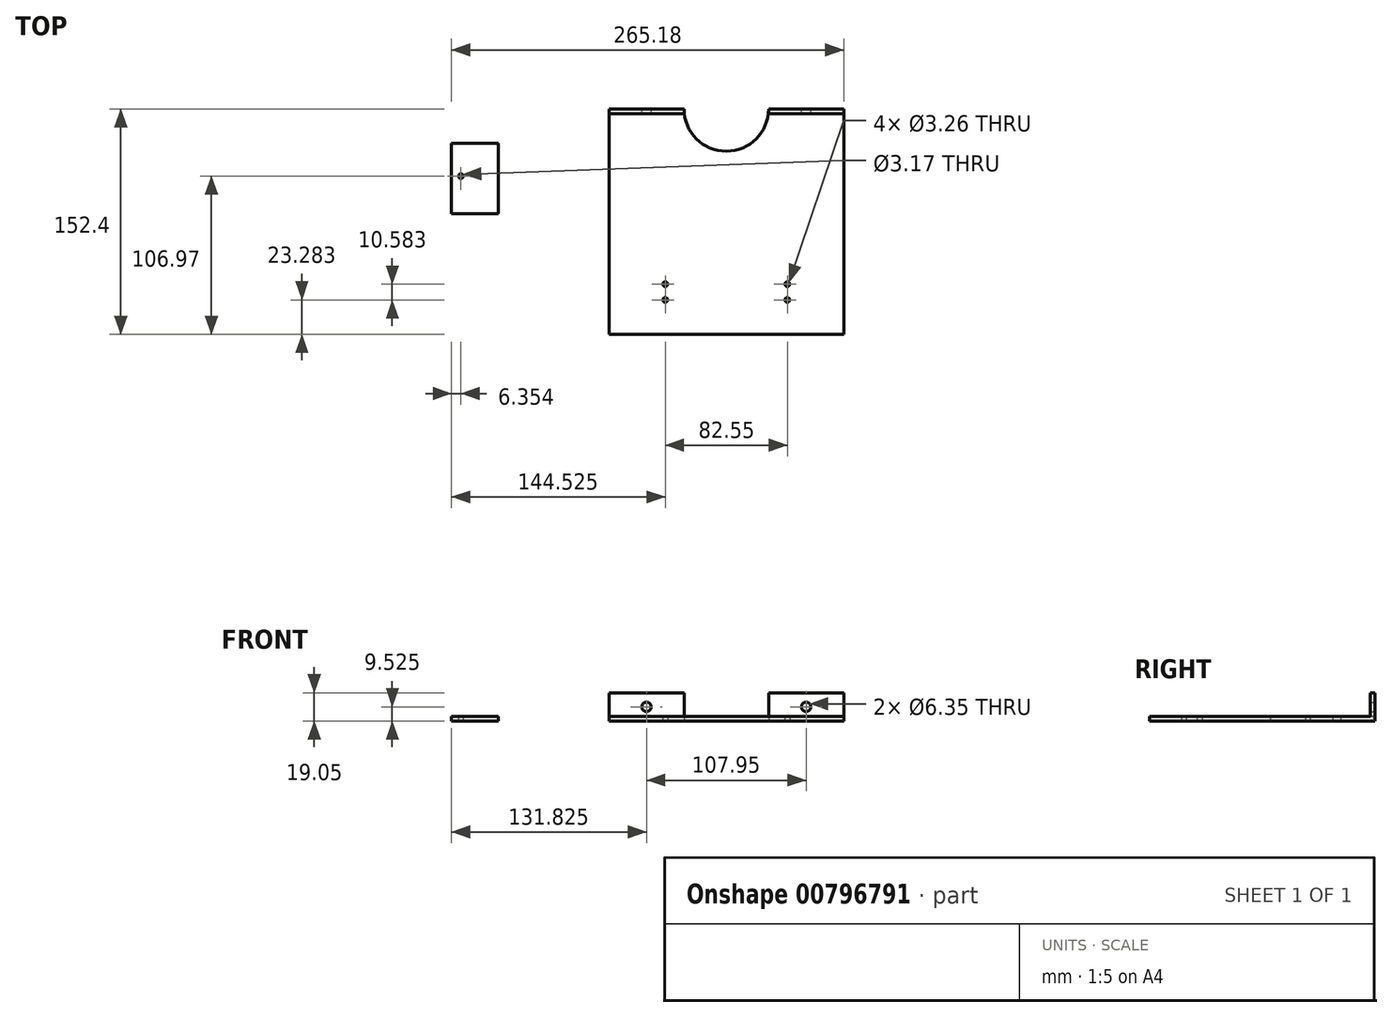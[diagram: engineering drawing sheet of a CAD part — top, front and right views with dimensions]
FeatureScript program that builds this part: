
annotation { "Feature Type Name" : "Feature", "Feature Type Description" : "" }
export const myFeature = defineFeature(function(context is Context, id is Id, definition is map)
    precondition{}
    {
        {
            var Q0;
            Q0=qCreatedBy(makeId("Top.planeOp"),FACE);
            var sketch = newSketch(context, id + "F0", { "sketchPlane" : qUnion([Q0])});
            skLineSegment(sketch, "E0.left", {"start": v(-79.38, 0) * mm, "end": v(-79.37, -152.4) * mm});
            skLineSegment(sketch, "E1.right", {"start": v(79.38, 0) * mm, "end": v(79.38, -152.4) * mm});
            skLineSegment(sketch, "E2", {"start": v(-79.37, -152.4) * mm, "end": v(79.37, -152.4) * mm});
            skArc(sketch, "E3", {"start": v(-28.58, 0) * mm, "mid": v(0, -28.58) * mm, "end": v(28.58, 0) * mm});
            skLineSegment(sketch, "E4", {"start": v(-79.38, 0) * mm, "end": v(-28.58, 0) * mm});
            skLineSegment(sketch, "E5", {"start": v(28.58, 0) * mm, "end": v(79.38, 0) * mm});
            skLineSegment(sketch, "E6", {"start": v(28.58, 0) * mm, "end": v(-28.58, 0) * mm, "construction": true});
            skSolve(sketch);
        }
        {
            var Q0;
            Q0=qCreatedBy(makeId("Front.planeOp"),FACE);
            var sketch = newSketch(context, id + "F1", { "sketchPlane" : qUnion([Q0])});
            skLineSegment(sketch, "E7.bottom", {"start": v(28.57, 19.05) * mm, "end": v(79.38, 19.05) * mm});
            skLineSegment(sketch, "E7.top", {"start": v(28.57, 0) * mm, "end": v(79.38, 0) * mm});
            skLineSegment(sketch, "E7.left", {"start": v(28.57, 19.05) * mm, "end": v(28.57, 0) * mm});
            skLineSegment(sketch, "E7.right", {"start": v(79.38, 19.05) * mm, "end": v(79.38, 0) * mm});
            skLineSegment(sketch, "E8.bottom", {"start": v(-79.38, 19.05) * mm, "end": v(-28.57, 19.05) * mm});
            skLineSegment(sketch, "E8.top", {"start": v(-79.38, 0) * mm, "end": v(-28.57, 0) * mm});
            skLineSegment(sketch, "E8.left", {"start": v(-79.38, 19.05) * mm, "end": v(-79.38, 0) * mm});
            skLineSegment(sketch, "E8.right", {"start": v(-28.57, 19.05) * mm, "end": v(-28.57, 0) * mm});
            skCircle(sketch, "E9", {"center": v(53.97, 9.53) * mm, "radius": 3.18 * mm});
            skCircle(sketch, "E10", {"center": v(-53.97, 9.52) * mm, "radius": 3.18 * mm});
            skLineSegment(sketch, "E11", {"start": v(53.97, 19.05) * mm, "end": v(53.97, 0) * mm, "construction": true});
            skLineSegment(sketch, "E12", {"start": v(79.38, 9.53) * mm, "end": v(28.57, 9.53) * mm, "construction": true});
            skLineSegment(sketch, "E13", {"start": v(-53.97, 19.05) * mm, "end": v(-53.97, 0) * mm, "construction": true});
            skLineSegment(sketch, "E14", {"start": v(-28.57, 9.52) * mm, "end": v(-79.38, 9.52) * mm, "construction": true});
            skSolve(sketch);
        }
        {
            var Q0;
            Q0=makeQuery(id+"F0.imprint","IMPRINT",FACE,{"disambiguationData":[TD([[makeQuery(id+"F0.imprint","IMPRINT",EDGE,{"derivedFrom":sQuery(id+"F0.wireOp",EDGE,"E0.left")}),1.0]])]});
            extrude(context, id + "F2", {"entities" : qUnion([Q0]), "depth" : 3.17 * mm, "offsetDistance" : 25.4 * mm});
        }
        {
            var Q0;
            Q0=makeQuery(id+"F1.imprint","IMPRINT",FACE,{"disambiguationData":[TD([[makeQuery(id+"F1.imprint","IMPRINT",EDGE,{"derivedFrom":sQuery(id+"F1.wireOp",EDGE,"E7.bottom")}),-1.0]])]});
            var Q1;
            Q1=makeQuery(id+"F1.imprint","IMPRINT",FACE,{"disambiguationData":[TD([[makeQuery(id+"F1.imprint","IMPRINT",EDGE,{"derivedFrom":sQuery(id+"F1.wireOp",EDGE,"E8.bottom")}),-1.0]])]});
            var Q2;
            Q2 = qSketchRegion(id + "F4", true);
            extrude(context, id + "F3", {"entities" : qUnion([Q0, Q1, Q2]), "operationType" : NewBodyOperationType.ADD, "depth" : 3.17 * mm, "offsetDistance" : 25.4 * mm});
        }
        {
            var Q0;
            Q0=qCreatedBy(makeId("Front.planeOp"),FACE);
            var sketch = newSketch(context, id + "F4", { "sketchPlane" : qUnion([Q0])});
            skCircle(sketch, "E15", {"center": v(-53.97, 11.11) * mm, "radius": 3.18 * mm});
            skCircle(sketch, "E16", {"center": v(53.97, 11.11) * mm, "radius": 3.18 * mm});
            skLineSegment(sketch, "E17", {"start": v(-53.97, 19.05) * mm, "end": v(-53.97, 3.18) * mm, "construction": true});
            skLineSegment(sketch, "E18", {"start": v(-79.38, 11.11) * mm, "end": v(-28.57, 11.11) * mm, "construction": true});
            skLineSegment(sketch, "E19", {"start": v(53.97, 19.05) * mm, "end": v(53.97, 3.18) * mm, "construction": true});
            skLineSegment(sketch, "E20", {"start": v(28.57, 11.11) * mm, "end": v(79.38, 11.11) * mm, "construction": true});
            skSolve(sketch);
        }
        {
            var Q0;
            Q0=qCreatedBy(makeId("Top.planeOp"),FACE);
            var sketch = newSketch(context, id + "F5", { "sketchPlane" : qUnion([Q0])});
            skLineSegment(sketch, "E21.bottom", {"start": v(-185.8, -23.2) * mm, "end": v(-154.05, -23.2) * mm});
            skLineSegment(sketch, "E21.top", {"start": v(-185.8, -70.83) * mm, "end": v(-154.05, -70.83) * mm});
            skLineSegment(sketch, "E21.left", {"start": v(-185.8, -23.2) * mm, "end": v(-185.8, -70.83) * mm});
            skLineSegment(sketch, "E21.right", {"start": v(-154.05, -23.2) * mm, "end": v(-154.05, -70.83) * mm});
            skCircle(sketch, "E22", {"center": v(-179.45, -45.43) * mm, "radius": 1.59 * mm});
            skCircle(sketch, "E23", {"center": v(-147.7, -45.43) * mm, "radius": 1.59 * mm});
            skLineSegment(sketch, "E24", {"start": v(-179.45, -45.43) * mm, "end": v(-179.45, -70.83) * mm, "construction": true});
            skLineSegment(sketch, "E25", {"start": v(-147.7, -45.43) * mm, "end": v(-147.7, -70.83) * mm, "construction": true});
            skLineSegment(sketch, "E26", {"start": v(-179.45, -45.43) * mm, "end": v(-147.7, -45.43) * mm, "construction": true});
            skLineSegment(sketch, "E27", {"start": v(-154.05, -45.43) * mm, "end": v(-147.7, -45.43) * mm, "construction": true});
            skLineSegment(sketch, "E28", {"start": v(-179.45, -45.43) * mm, "end": v(-185.8, -45.43) * mm, "construction": true});
            skSolve(sketch);
        }
        {
            var Q0;
            Q0=makeQuery(id+"F5.imprint","IMPRINT",FACE,{"disambiguationData":[TD([[makeQuery(id+"F5.imprint","IMPRINT",EDGE,{"derivedFrom":sQuery(id+"F5.wireOp",EDGE,"wrMeZvNA-k4aE-4lbz-n74W-sSAz8d7ppq8d.bottom")}),-1.0]])]});
            var Q1;
            Q1=makeQuery(id+"F5.imprint","IMPRINT",FACE,{"disambiguationData":[TD([[makeQuery(id+"F5.imprint","IMPRINT",EDGE,{"derivedFrom":sQuery(id+"F5.wireOp",EDGE,"E21.bottom")}),-1.0]])]});
            extrude(context, id + "F6", {"entities" : qUnion([Q0, Q1]), "depth" : 3.17 * mm, "offsetDistance" : 25.4 * mm});
        }
        {
            var Q0;
            Q0=qCreatedBy(makeId("Top.planeOp"),FACE);
            var sketch = newSketch(context, id + "F7", { "sketchPlane" : qUnion([Q0])});
            skLineSegment(sketch, "E29.bottom", {"start": v(-53.97, -107.95) * mm, "end": v(-28.57, -107.95) * mm, "construction": true});
            skLineSegment(sketch, "E29.top", {"start": v(-53.97, -139.7) * mm, "end": v(-28.57, -139.7) * mm, "construction": true});
            skLineSegment(sketch, "E29.left", {"start": v(-53.97, -107.95) * mm, "end": v(-53.97, -139.7) * mm, "construction": true});
            skLineSegment(sketch, "E29.right", {"start": v(-28.57, -107.95) * mm, "end": v(-28.57, -139.7) * mm, "construction": true});
            skLineSegment(sketch, "E30.bottom", {"start": v(28.58, -107.95) * mm, "end": v(53.98, -107.95) * mm, "construction": true});
            skLineSegment(sketch, "E30.top", {"start": v(28.58, -139.7) * mm, "end": v(53.98, -139.7) * mm, "construction": true});
            skLineSegment(sketch, "E30.left", {"start": v(28.58, -107.95) * mm, "end": v(28.58, -139.7) * mm, "construction": true});
            skLineSegment(sketch, "E30.right", {"start": v(53.98, -107.95) * mm, "end": v(53.98, -139.7) * mm, "construction": true});
            skLineSegment(sketch, "E31", {"start": v(-53.97, -107.95) * mm, "end": v(-79.37, -107.95) * mm, "construction": true});
            skLineSegment(sketch, "E32", {"start": v(53.98, -107.95) * mm, "end": v(79.38, -107.95) * mm, "construction": true});
            skLineSegment(sketch, "E33", {"start": v(53.98, -139.7) * mm, "end": v(53.98, -152.4) * mm, "construction": true});
            skLineSegment(sketch, "E34", {"start": v(-53.97, -139.7) * mm, "end": v(-53.97, -152.4) * mm, "construction": true});
            skCircle(sketch, "E35", {"center": v(-41.27, -118.53) * mm, "radius": 1.63 * mm});
            skCircle(sketch, "E36", {"center": v(-41.27, -129.12) * mm, "radius": 1.63 * mm});
            skCircle(sketch, "E37", {"center": v(41.28, -118.53) * mm, "radius": 1.63 * mm});
            skCircle(sketch, "E38", {"center": v(41.28, -129.12) * mm, "radius": 1.63 * mm});
            skLineSegment(sketch, "E39", {"start": v(-41.27, -107.95) * mm, "end": v(-41.27, -118.53) * mm, "construction": true});
            skLineSegment(sketch, "E40", {"start": v(-41.27, -118.53) * mm, "end": v(-41.27, -129.12) * mm, "construction": true});
            skLineSegment(sketch, "E41", {"start": v(-41.27, -129.12) * mm, "end": v(-41.27, -139.7) * mm, "construction": true});
            skLineSegment(sketch, "E42", {"start": v(41.28, -107.95) * mm, "end": v(41.28, -118.53) * mm, "construction": true});
            skLineSegment(sketch, "E43", {"start": v(41.28, -118.53) * mm, "end": v(41.28, -129.12) * mm, "construction": true});
            skLineSegment(sketch, "E44", {"start": v(41.28, -129.12) * mm, "end": v(41.28, -139.7) * mm, "construction": true});
            skSolve(sketch);
        }
        {
            var Q0;
            Q0 = qSketchRegion(id + "F7", true);
            extrude(context, id + "F8", {"entities" : qUnion([Q0]), "operationType" : NewBodyOperationType.REMOVE, "depth" : 39.37 * mm, "offsetDistance" : 25.4 * mm});
        }
    });
